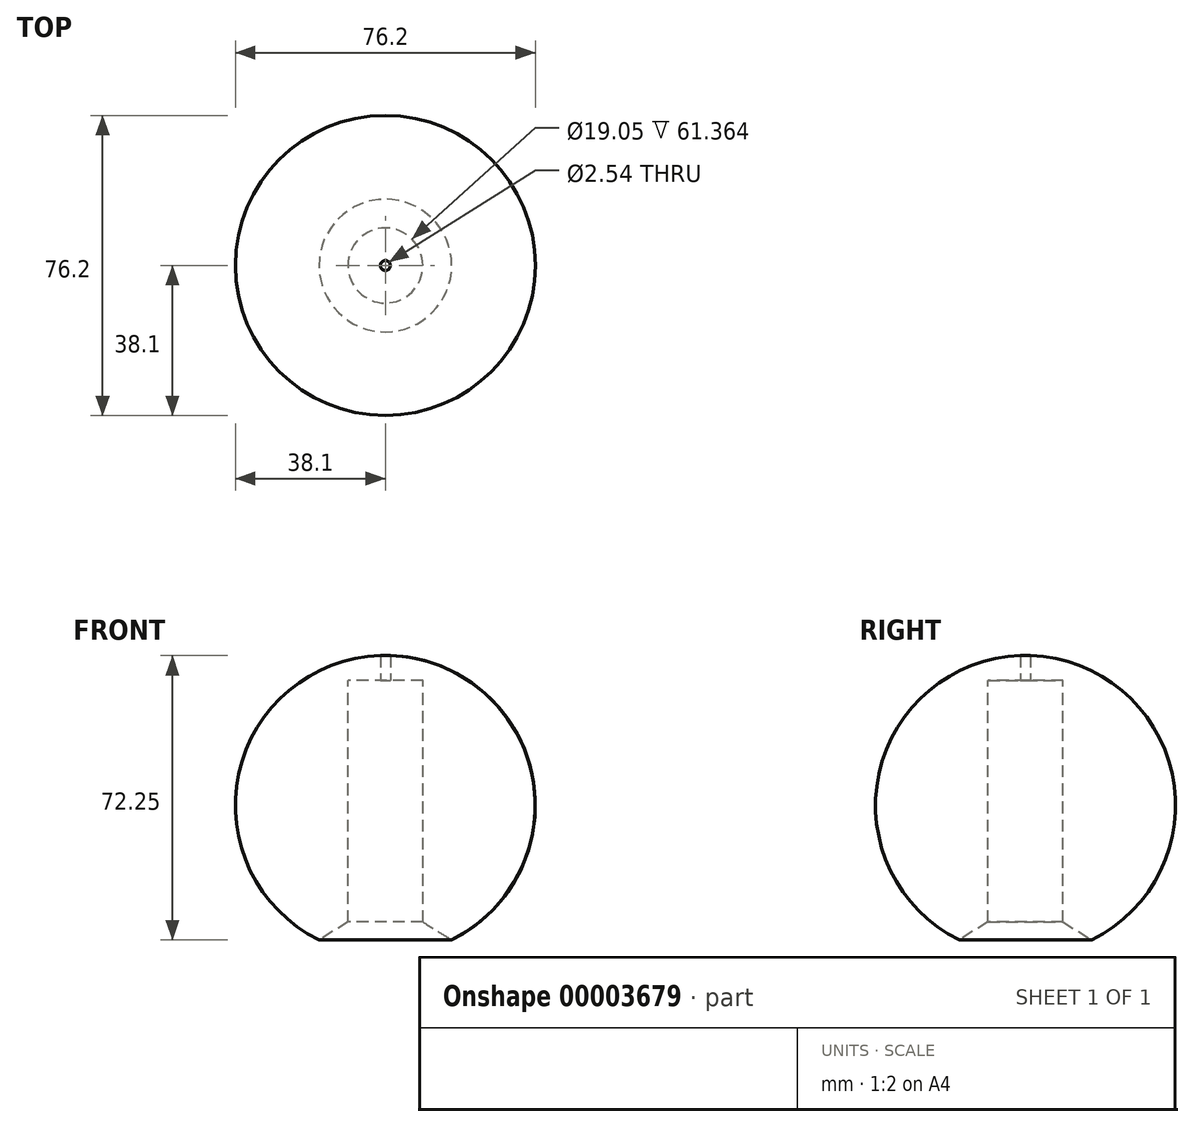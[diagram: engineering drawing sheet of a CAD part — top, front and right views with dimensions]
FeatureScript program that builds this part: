
annotation { "Feature Type Name" : "Feature", "Feature Type Description" : "" }
export const myFeature = defineFeature(function(context is Context, id is Id, definition is map)
    precondition{}
    {
        {
            var Q0;
            Q0=qCreatedBy(makeId("Front.planeOp"),FACE);
            var sketch = newSketch(context, id + "F0", { "sketchPlane" : qUnion([Q0])});
            skLineSegment(sketch, "E0", {"start": v(0, 38.1) * mm, "end": v(0, -49.61) * mm});
            skArc(sketch, "E1", {"start": v(0, -38.1) * mm, "mid": v(38.1, 0) * mm, "end": v(0, 38.1) * mm});
            skSolve(sketch);
        }
        {
            var Q0;
            Q0=makeQuery(id+"F0.imprint","IMPRINT",FACE,{"disambiguationData":[TD([[makeQuery(id+"F0.imprint","IMPRINT",EDGE,{"derivedFrom":sQuery(id+"F0.wireOp",EDGE,"E0")}),1.0]])]});
            var Q1;
            Q1=sQuery(id+"F0.wireOp",EDGE,"E0");
            revolve(context, id + "F1", {"entities" : qUnion([Q0]), "axis" : qUnion([Q1]), "revolveType" : RevolveType.FULL});
        }
        {
            var Q0;
            Q0=qCreatedBy(makeId("Top.planeOp"),FACE);
            var sketch = newSketch(context, id + "F2", { "sketchPlane" : qUnion([Q0])});
            skCircle(sketch, "E2", {"center": v(0, 0) * mm, "radius": 9.53 * mm});
            skSolve(sketch);
        }
        {
            var Q0;
            Q0 = qSketchRegion(id + "F2", true);
            extrude(context, id + "F3", {"entities" : qUnion([Q0]), "operationType" : NewBodyOperationType.REMOVE, "oppositeDirection" : true, "depth" : 107.67 * mm});
        }
        {
            var Q0;
            Q0 = qSketchRegion(id + "F2", true);
            extrude(context, id + "F4", {"entities" : qUnion([Q0]), "operationType" : NewBodyOperationType.REMOVE, "depth" : 31.75 * mm});
        }
        {
            var Q0;
            Q0=makeQuery(id+"F3.boolean.opBoolean","INTERSECT",EDGE,{"derivedFrom":[makeQuery(id+"F1.opRevolve","SWEPT_FACE",FACE,{"disambiguationData":[OSD([sQuery(id+"F0.wireOp",EDGE,"E1")])]}),makeQuery(id+"F3.opExtrude","SWEPT_FACE",FACE,{"disambiguationData":[OSD([sQuery(id+"F2.wireOp",EDGE,"E2")])]})]});
            chamfer(context, id + "F5", {"entities" : qUnion([Q0]), "width" : 5.08 * mm, "tangentPropagation" : true});
        }
        {
            var Q0;
            Q0=makeQuery(id+"F4.boolean.opBoolean","COPY",FACE,{"derivedFrom":makeQuery(id+"F4.opExtrude","CAP_FACE",FACE,{"disambiguationData":[OSD([sQuery(id+"F2.wireOp",EDGE,"E2")])],"isStart":false})});
            var sketch = newSketch(context, id + "F6", { "sketchPlane" : qUnion([Q0])});
            skCircle(sketch, "E3", {"center": v(0, 0) * mm, "radius": 1.27 * mm});
            skSolve(sketch);
        }
        {
            var Q0;
            Q0 = qSketchRegion(id + "F6", true);
            extrude(context, id + "F7", {"entities" : qUnion([Q0]), "operationType" : NewBodyOperationType.REMOVE, "endBound" : BoundingType.THROUGH_ALL, "oppositeDirection" : true, "depth" : 25.4 * mm});
        }
    });
